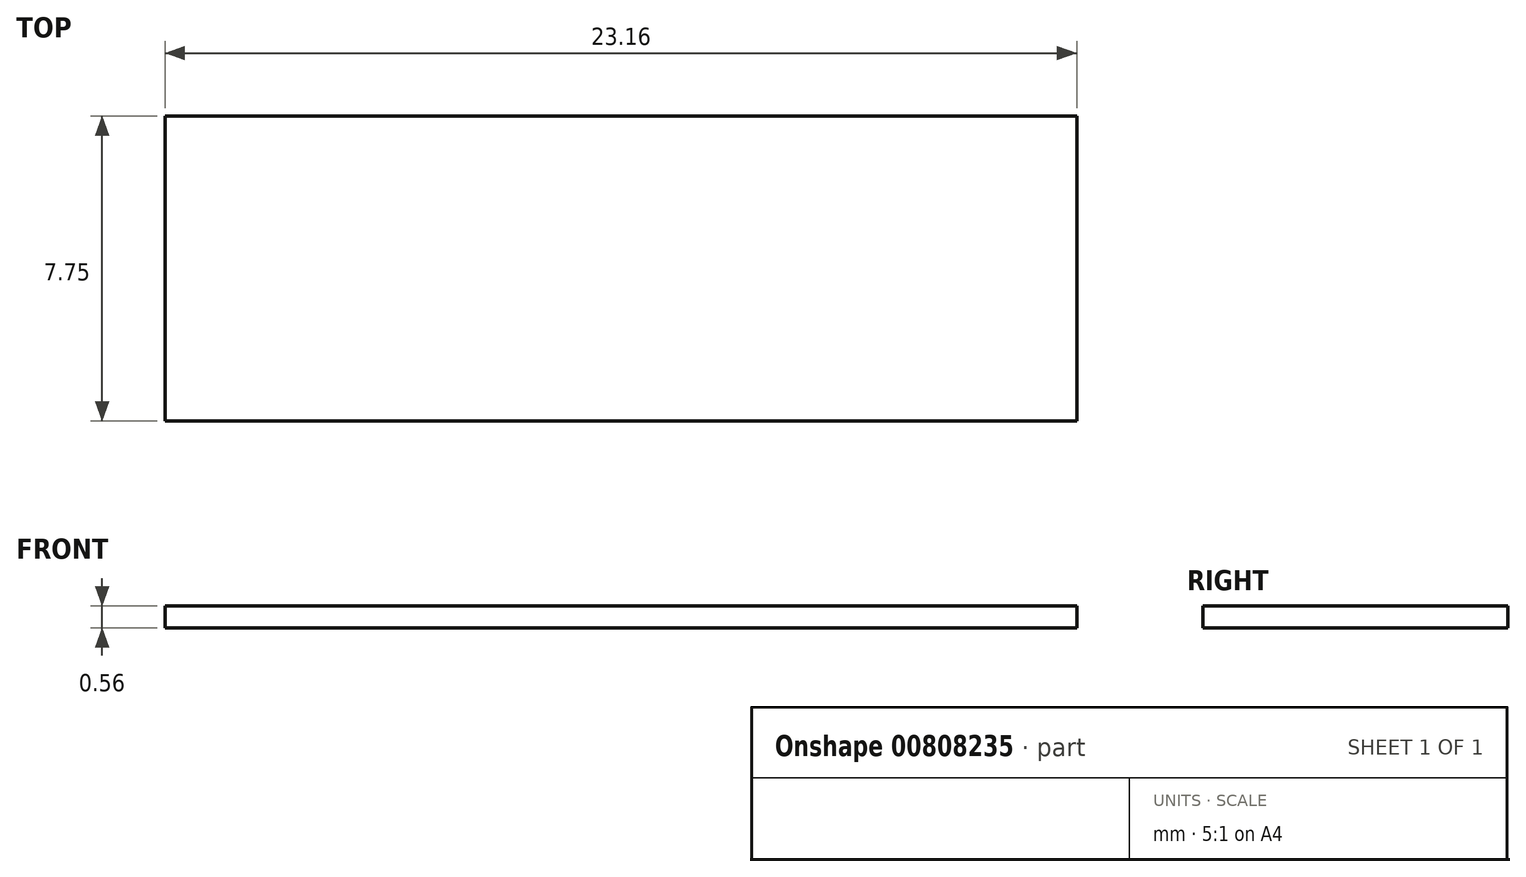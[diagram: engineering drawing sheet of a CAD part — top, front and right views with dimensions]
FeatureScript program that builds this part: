
annotation { "Feature Type Name" : "Feature", "Feature Type Description" : "" }
export const myFeature = defineFeature(function(context is Context, id is Id, definition is map)
    precondition{}
    {
        {
            var Q0;
            Q0=qCreatedBy(makeId("Top.planeOp"),FACE);
            var sketch = newSketch(context, id + "F0", { "sketchPlane" : qUnion([Q0])});
            skLineSegment(sketch, "E0.bottom", {"start": v(-0.5, 0) * mm, "end": v(-23.67, 0) * mm});
            skLineSegment(sketch, "E0.top", {"start": v(-0.5, -7.75) * mm, "end": v(-23.67, -7.75) * mm});
            skLineSegment(sketch, "E0.left", {"start": v(-0.5, 0) * mm, "end": v(-0.5, -7.75) * mm});
            skLineSegment(sketch, "E0.right", {"start": v(-23.67, 0) * mm, "end": v(-23.67, -7.75) * mm});
            skSolve(sketch);
        }
        {
            var Q0;
            Q0=makeQuery(id+"F0.imprint","IMPRINT",FACE,{"disambiguationData":[TD([[makeQuery(id+"F0.imprint","IMPRINT",EDGE,{"derivedFrom":sQuery(id+"F0.wireOp",EDGE,"E0.bottom")}),1.0]])]});
            extrude(context, id + "F1", {"entities" : qUnion([Q0]), "depth" : 0.56 * mm, "offsetDistance" : 25.4 * mm});
        }
    });
